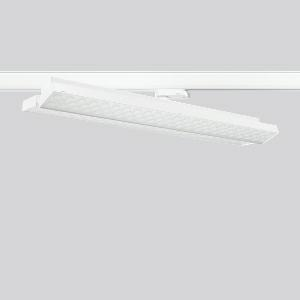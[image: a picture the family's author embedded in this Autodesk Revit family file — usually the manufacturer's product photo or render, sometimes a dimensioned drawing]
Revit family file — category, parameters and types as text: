
# Revit family: tx-move_742161_002_2_76_9baf
name_source: partatom
category: Lighting Fixtures
units: mm (PartAtom-declared; Revit-internal decimal feet)

## family parameters
Cut with Voids When Loaded = No
Host = Face
Light Source = No
Part Type = Normal
Room Calculation Point = No
Round Connector Dimension = Use Diameter
Shared = No

## types (1)
- MultiLumen 1 (1 x LED Modul 927, 2100 lm, 2700)
    Apparent Load = 38 VA
    CIE Flux Codes = 90 97 99 100 100
    Color Rendering = 92
    Color Temperature = 2700
    Default Elevation = 1800 mm
    Description = Series: TX-MOVE
Multifunctional surface-mounted spotlight for area lighting. Very flat design. Housing: sheet steel, powder-coated. Rotation range: 356°. Swivel range: 90°. Consistent alignment possible with visible tilt scale. High-efficiency LED units with optimum light control thanks to clear plastic (PC) lens optics. Spezielle Mikrostrukturen reduzieren Gelbsaum. Symmetrical light distribution. Best colour rendering with CRI >90 for fresh products and coloured textiles. With adapter for RZB 3-circuit DALI tracks. Suitable for Track on ceiling. MultiLumen: Luminous flux adjustable in 3 steps. Factory setting is the highest luminous flux. Environmentally friendly and resource-saving due to replaceable and recyclable components. Very good glare control, ideal for till areas. 
Colour: traffic white, matt (RAL 9016)
Length: 570 mm
Width: 119 mm
Height: 88 mm
Lamp: LED
Socket: without socket
Colour temperature: 2700K
Colour rendering index (CRI): 90
System power: 38 W
Rated luminous flux: 4200 lm
Luminous efficiency: 111 lm/W
System power 2: 51 W
Rated luminous flux 2: 5500 lm
Luminous efficiency 2: 108 lm/W
System power 3: 62 W
Rated luminous flux 3: 6500 lm
Luminous efficiency 3: 105 lm/W
Control gear: Dimmable EVG, DALI
Protection class: I
Type of protection: IP 20
    Height = 75 mm
    Lamp = 1 x LED Modul 927
    Lamp Light Flux = 2100 lm
    Lamp count = 1
    Length = 569 mm
    Lifetime = 50000 h
    Luminous efficacy = 111 lm/W
    Manufacturer = RZB
    ModVariant = No
    Model = 742161.002.2.76
    Mounting Place = Ceiling
    Mounting Type = Surface mounted
    Number of Poles = 1
    OnlyDefault = Yes
    Power Factor = 1
    Product Name = TX-MOVE
    Product group = Track mounted projectors
    ProductGroupID = 301
    Protection Class = Protection class I
    Protection Degree = IP 20
    RLX_Detail_Level = 1
    RLX_Emergency_Light_Flux = 0 lm
    RLX_Emergency_Type = 0
    RLX_Emergency_Type_DB = No
    RlxData = <blob elided: 31305 chars, md5=f0a39e7b>
    Socket = socket
    Standby Power = 0 W
    System Light Flux = 4200 lm
    System Power = 38 W
    Type Comments = MultiLumen 1
    Type Image = 742162.002.jpg
    URL = http://relux.com
    VarID = multilumen_1
    Voltage = 0 V
    Weight = 0.00 kg
    Width = 119 mm

## geometry (parser evidence)
native form markers: Blend x4, Sweep x15
no freeform markers — native parametric forms only
